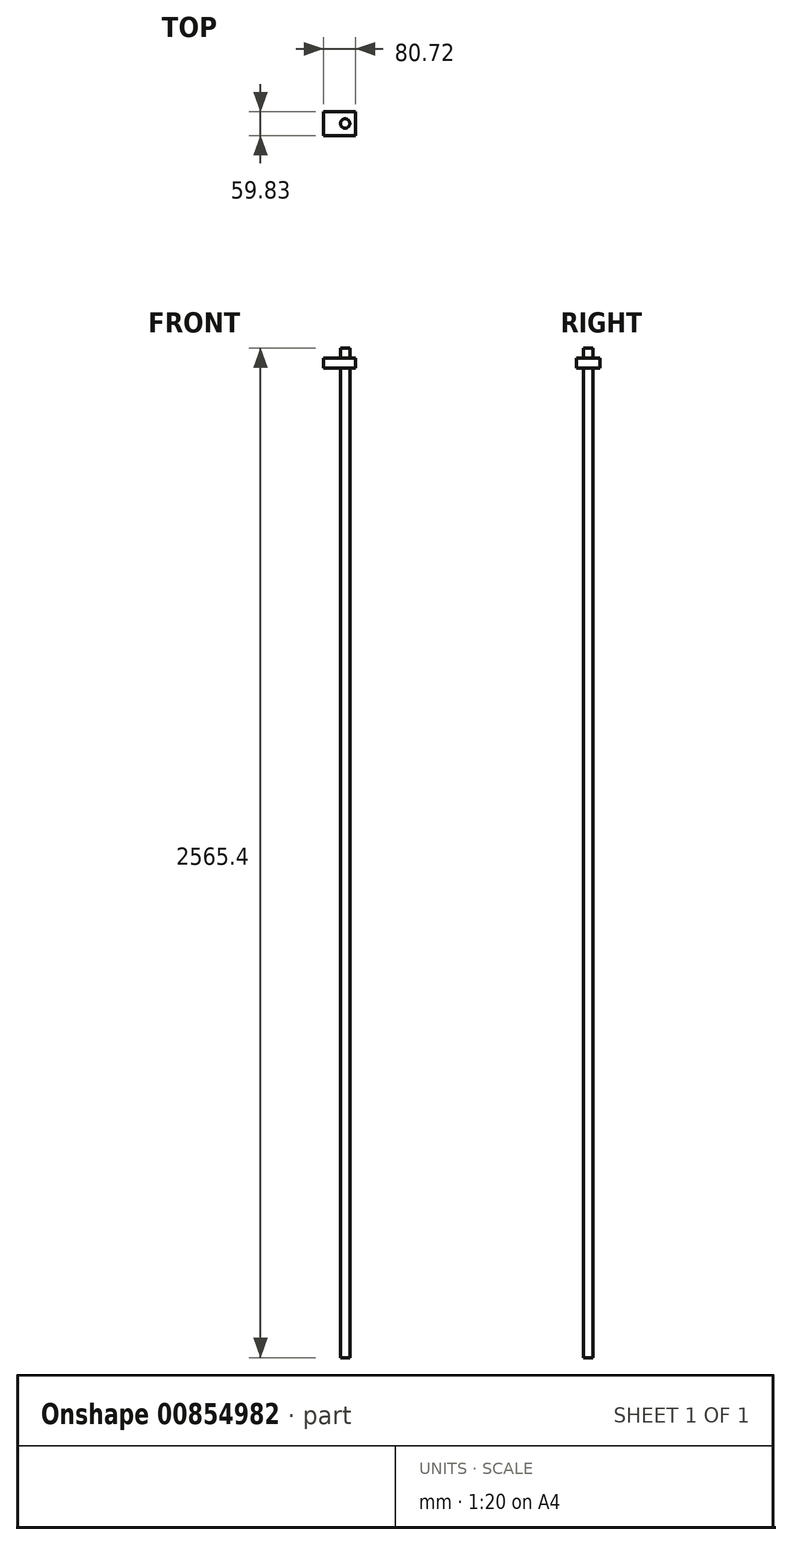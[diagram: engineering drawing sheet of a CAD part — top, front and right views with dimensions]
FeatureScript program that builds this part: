
annotation { "Feature Type Name" : "Feature", "Feature Type Description" : "" }
export const myFeature = defineFeature(function(context is Context, id is Id, definition is map)
    precondition{}
    {
        {
            var Q0;
            Q0=qCreatedBy(makeId("Top.planeOp"),FACE);
            var sketch = newSketch(context, id + "F0", { "sketchPlane" : qUnion([Q0])});
            skLineSegment(sketch, "E0.bottom", {"start": v(4.45, -21.81) * mm, "end": v(-76.27, -21.81) * mm});
            skLineSegment(sketch, "E0.top", {"start": v(4.45, 38.02) * mm, "end": v(-76.27, 38.02) * mm});
            skLineSegment(sketch, "E0.left", {"start": v(4.45, -21.81) * mm, "end": v(4.45, 38.02) * mm});
            skLineSegment(sketch, "E0.right", {"start": v(-76.27, -21.81) * mm, "end": v(-76.27, 38.02) * mm});
            skSolve(sketch);
        }
        {
            var Q0;
            Q0 = qSketchRegion(id + "F0", true);
            extrude(context, id + "F1", {"entities" : qUnion([Q0]), "depth" : 25.4 * mm, "offsetDistance" : 25.4 * mm});
        }
        {
            var Q0;
            Q0=makeQuery(id+"F1.opExtrude","CAP_FACE",FACE,{"disambiguationData":[OSD([sQuery(id+"F0.wireOp",EDGE,"E0.bottom"),sQuery(id+"F0.wireOp",EDGE,"E0.top"),sQuery(id+"F0.wireOp",EDGE,"E0.left"),sQuery(id+"F0.wireOp",EDGE,"E0.right")])],"isStart":false});
            var sketch = newSketch(context, id + "F2", { "sketchPlane" : qUnion([Q0])});
            skCircle(sketch, "E1", {"center": v(-21.64, 8.48) * mm, "radius": 11.95 * mm});
            skSolve(sketch);
        }
        {
            var Q0;
            Q0 = qSketchRegion(id + "F2", true);
            extrude(context, id + "F3", {"entities" : qUnion([Q0]), "operationType" : NewBodyOperationType.ADD, "depth" : 25.4 * mm, "offsetDistance" : 25.4 * mm, "hasSecondDirection" : true, "secondDirectionOppositeDirection" : true, "secondDirectionDepth" : 2540 * mm});
        }
    });
